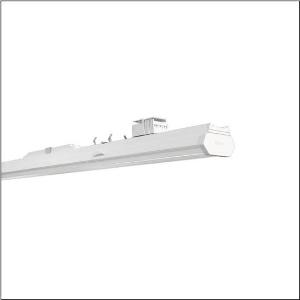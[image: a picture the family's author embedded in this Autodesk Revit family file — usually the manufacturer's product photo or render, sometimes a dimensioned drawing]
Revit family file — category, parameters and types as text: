
# Revit family: licross_r__11_protected_ho_51ts12dn5dxl_8709
name_source: partatom
category: Lighting Fixtures
units: mm (PartAtom-declared; Revit-internal decimal feet)

## family parameters
Cut with Voids When Loaded = No
Host = Face
Light Source = No
Part Type = Normal
Room Calculation Point = No
Round Connector Dimension = Use Diameter
Shared = No

## types (1)
- --- (1 x LED, 13380 lm, 86.1 W, 5000K)
    Apparent Load = 86 VA
    CIE Flux Codes = 54 82 95 97 100
    Color Rendering = 80
    Color Temperature = 5000K
    Default Elevation = 1800 mm
    Description = Licross® 11 Protected HO, luminaire insert, of sheet steel, galvanised, coil coated, white, length: 1.500mm, width: 90mm, height: 101mm, LED rated luminous flux: 13.380lm, light colour: 850, control gear: DALI 2, control gear: ECG DALI, with plug, 5-pole, with phase selection, mains connection: 220..240V, AC, 50/60Hz, rated input power: 86W, halogen-free wiring, primary optical cover: cover, of PMMA, light emission: direct distribution, primary light characteristic: symmetric, protection rating (complete): IP50, insulation class (complete): insulation class I (protective earthing), certification: CE, ENEC, VDE, UKCA, protection symbol: D if used in an environment with non-conductive dust loads with corresponding accessories, impact resistance: IK06, permissible ambient temperature for indoor applications: -25..+35°C, reducing of maximum allowable ambient temperature of 5°C with ceiling mounting, corresponds to IFS (International Featured Standards) requirements for safety and quality in the food industry, LABS conformity tested according to VDMA 24364:2018-05, packaging unit: 1 piece
    Height = 92 mm
    Lamp = 1 x LED
    Lamp Light Flux = 13380 lm
    Lamp Power = 86.1 W
    Lamp count = 1
    Length = 1500 mm
    Luminous efficacy = 155 lm/W
    Manufacturer = Siteco
    ModVariant = No
    Model = 51TS12DN5DXL
    Mounting Place = Ceiling
    Mounting Type = Pendant
    Number of Poles = 1
    OnlyDefault = Yes
    Power Factor = 1
    Product Name = Licross® 11 Protected HO
    Product group = luminaire insert
    ProductGroupID = 901
    Protection Class = Protection class I
    Protection Degree = IP 50
    RLX_Detail_Level = 1
    RLX_Emergency_Light_Flux = 0 lm
    RLX_Emergency_Type = 0
    RLX_Emergency_Type_DB = No
    RlxData = <blob elided: 24101 chars, md5=fa6aa6d0>
    Socket = socket
    Standby Power = 0 W
    System Light Flux = 13380 lm
    System Power = 86 W
    Type Comments = factory setting: luminous flux: 100 % | dim-lin: 254 | 485 mA
    Type Image = l_1256145.jpg
    URL = http://relux.com
    VarID = @adj_143853
    Voltage = 0 V
    Weight = 0.00 kg
    Width = 88 mm

## geometry (parser evidence)
native form markers: Blend x4, Sweep x11
no freeform markers — native parametric forms only
